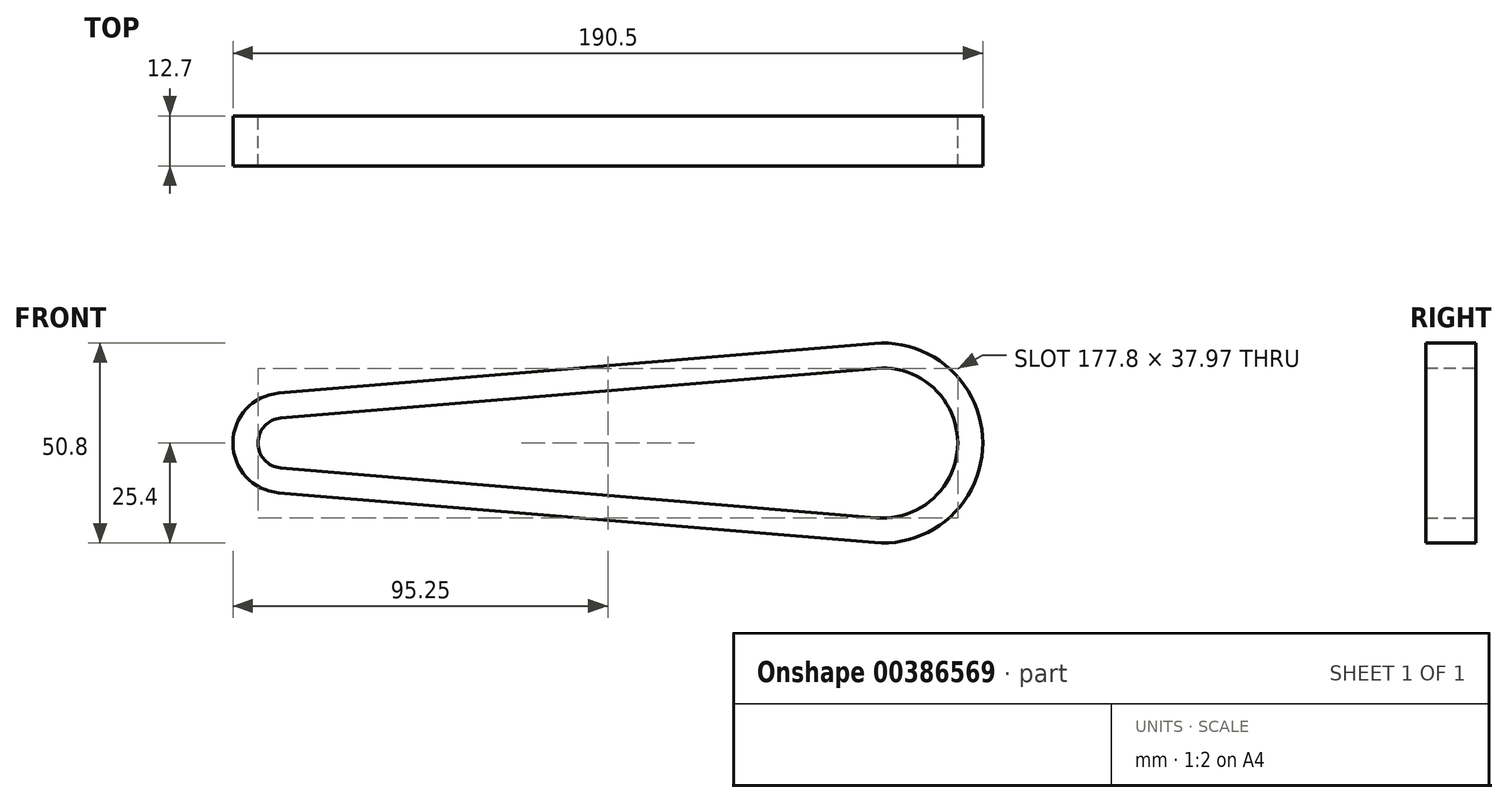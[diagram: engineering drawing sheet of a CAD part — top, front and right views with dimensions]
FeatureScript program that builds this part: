
annotation { "Feature Type Name" : "Feature", "Feature Type Description" : "" }
export const myFeature = defineFeature(function(context is Context, id is Id, definition is map)
    precondition{}
    {
        {
            var Q0;
            Q0=qCreatedBy(makeId("Front.planeOp"),FACE);
            var sketch = newSketch(context, id + "F0", { "sketchPlane" : qUnion([Q0])});
            skArc(sketch, "E0", {"start": v(-2.12, -25.31) * mm, "mid": v(25.4, 0) * mm, "end": v(-2.12, 25.31) * mm});
            skArc(sketch, "E1", {"start": v(-153.46, 12.66) * mm, "mid": v(-165.1, 0) * mm, "end": v(-153.46, -12.66) * mm});
            skLineSegment(sketch, "E2", {"start": v(-153.46, 12.66) * mm, "end": v(-2.12, 25.31) * mm});
            skLineSegment(sketch, "E3", {"start": v(-2.12, -25.31) * mm, "end": v(-153.46, -12.66) * mm});
            skLineSegment(sketch, "E4.0", {"start": v(-152.93, 6.33) * mm, "end": v(-1.59, 18.98) * mm});
            skArc(sketch, "E4.1", {"start": v(-152.93, 6.33) * mm, "mid": v(-158.75, 0) * mm, "end": v(-152.93, -6.33) * mm});
            skLineSegment(sketch, "E4.2", {"start": v(-1.59, -18.98) * mm, "end": v(-152.93, -6.33) * mm});
            skArc(sketch, "E4.3", {"start": v(-1.59, -18.98) * mm, "mid": v(19.05, 0) * mm, "end": v(-1.59, 18.98) * mm});
            skSolve(sketch);
        }
        {
            var Q0;
            Q0=makeQuery(id+"F0.imprint","IMPRINT",FACE,{"disambiguationData":[TD([[makeQuery(id+"F0.imprint","IMPRINT",EDGE,{"derivedFrom":sQuery(id+"F0.wireOp",EDGE,"E0")}),1.0]])]});
            extrude(context, id + "F1", {"entities" : qUnion([Q0]), "depth" : 12.7 * mm});
        }
    });
